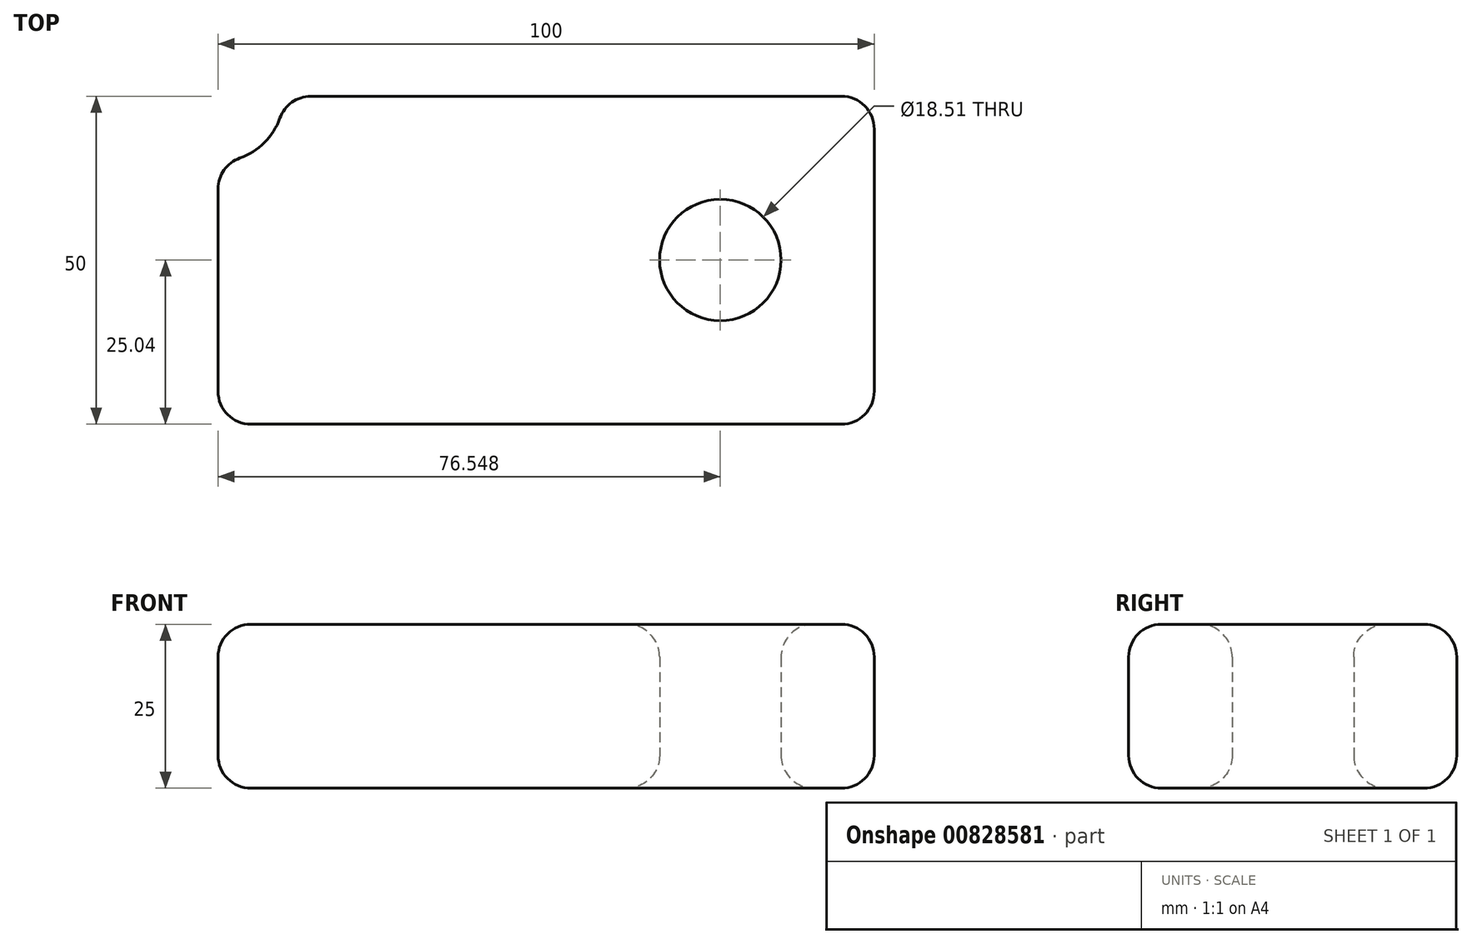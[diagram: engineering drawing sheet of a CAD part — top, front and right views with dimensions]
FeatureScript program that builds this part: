
annotation { "Feature Type Name" : "Feature", "Feature Type Description" : "" }
export const myFeature = defineFeature(function(context is Context, id is Id, definition is map)
    precondition{}
    {
        {
            var Q0;
            Q0=qCreatedBy(makeId("Top.planeOp"),FACE);
            var sketch = newSketch(context, id + "F0", { "sketchPlane" : qUnion([Q0])});
            skLineSegment(sketch, "E0.bottom", {"start": v(50, 25) * mm, "end": v(-50, 25) * mm});
            skLineSegment(sketch, "E0.top", {"start": v(50, -25) * mm, "end": v(-50, -25) * mm});
            skLineSegment(sketch, "E0.left", {"start": v(50, 25) * mm, "end": v(50, -25) * mm});
            skLineSegment(sketch, "E0.right", {"start": v(-50, 25) * mm, "end": v(-50, -25) * mm});
            skPoint(sketch, "E0.middle", {"position": v(0, 0) * mm});
            skCircle(sketch, "E1", {"center": v(-50, 25) * mm, "radius": 10 * mm});
            skCircle(sketch, "E2", {"center": v(26.55, 0.04) * mm, "radius": 9.26 * mm});
            skSolve(sketch);
        }
        {
            var Q0;
            {var subQ1=sQuery(id+"F0.wireOp",EDGE,"E0.top");Q0=makeQuery(id+"F0.imprint","IMPRINT",FACE,{"disambiguationData":[TD([[makeQuery(id+"F0.imprint","IMPRINT",EDGE,{"derivedFrom":subQ1}),-1.0]])]});}
            extrude(context, id + "F1", {"entities" : qUnion([Q0]), "depth" : 25 * mm, "offsetDistance" : 25 * mm});
        }
        {
            var Q0;
            Q0=makeQuery(id+"F1.opExtrude","CAP_FACE",FACE,{"disambiguationData":[OSD([sQuery(id+"F0.wireOp",EDGE,"E0.bottom"),sQuery(id+"F0.wireOp",EDGE,"E0.top"),sQuery(id+"F0.wireOp",EDGE,"E0.left"),sQuery(id+"F0.wireOp",EDGE,"E0.right"),sQuery(id+"F0.wireOp",EDGE,"E1"),sQuery(id+"F0.wireOp",EDGE,"E2")])],"isStart":false});
            var Q1;
            Q1=makeQuery(id+"F1.opExtrude","CAP_EDGE",EDGE,{"disambiguationData":[OSD([sQuery(id+"F0.wireOp",EDGE,"E0.bottom")])],"isStart":true});
            var Q2;
            Q2=makeQuery(id+"F1.opExtrude","CAP_EDGE",EDGE,{"disambiguationData":[OSD([sQuery(id+"F0.wireOp",EDGE,"E1")])],"isStart":true});
            var Q3;
            Q3=makeQuery(id+"F1.opExtrude","CAP_EDGE",EDGE,{"disambiguationData":[OSD([sQuery(id+"F0.wireOp",EDGE,"E0.left")])],"isStart":true});
            var Q4;
            Q4=makeQuery(id+"F1.opExtrude","CAP_EDGE",EDGE,{"disambiguationData":[OSD([sQuery(id+"F0.wireOp",EDGE,"E0.top")])],"isStart":true});
            var Q5;
            Q5=makeQuery(id+"F1.opExtrude","CAP_EDGE",EDGE,{"disambiguationData":[OSD([sQuery(id+"F0.wireOp",EDGE,"E0.right")])],"isStart":true});
            var Q6;
            Q6=makeQuery(id+"F1.opExtrude","CAP_EDGE",EDGE,{"disambiguationData":[OSD([sQuery(id+"F0.wireOp",EDGE,"E2")])],"isStart":true});
            fillet(context, id + "F2", {"entities" : qUnion([Q0, Q1, Q2, Q3, Q4, Q5, Q6]), "radius" : 5 * mm, "tangentPropagation" : true, "allowEdgeOverflow" : false});
        }
        {
            var Q0;
            Q0=makeQuery(id+"F1.opExtrude","SWEPT_EDGE",EDGE,{"disambiguationData":[OSD([sQuery(id+"F0.wireOp",EDGE,"E0.right"),sQuery(id+"F0.wireOp",EDGE,"E1")])]});
            var Q1;
            Q1=makeQuery(id+"F1.opExtrude","SWEPT_EDGE",EDGE,{"disambiguationData":[OSD([sQuery(id+"F0.wireOp",EDGE,"E0.bottom"),sQuery(id+"F0.wireOp",EDGE,"E1")])]});
            var Q2;
            Q2=makeQuery(id+"F1.opExtrude","SWEPT_EDGE",EDGE,{"disambiguationData":[OSD([sQuery(id+"F0.wireOp",EDGE,"E0.top"),sQuery(id+"F0.wireOp",EDGE,"E0.right")])]});
            var Q3;
            Q3=makeQuery(id+"F1.opExtrude","SWEPT_EDGE",EDGE,{"disambiguationData":[OSD([sQuery(id+"F0.wireOp",EDGE,"E0.bottom"),sQuery(id+"F0.wireOp",EDGE,"E0.left")])]});
            var Q4;
            Q4=makeQuery(id+"F1.opExtrude","SWEPT_EDGE",EDGE,{"disambiguationData":[OSD([sQuery(id+"F0.wireOp",EDGE,"E0.top"),sQuery(id+"F0.wireOp",EDGE,"E0.left")])]});
            fillet(context, id + "F3", {"entities" : qUnion([Q0, Q1, Q2, Q3, Q4]), "radius" : 5 * mm, "tangentPropagation" : true, "allowEdgeOverflow" : false});
        }
    });
